# Revit family: Toilet_Seat-Elongated_Closed_Front-KOHLER-PATIO-K-10614IN-1
name_source: partatom
category: Specialty Equipment
units: mm (PartAtom-declared; Revit-internal decimal feet)

## family parameters
Cut with Voids When Loaded = No
Host = Face
OmniClass Number = 23.31.19.19
OmniClass Title = Water Closets
Part Type = Normal
Room Calculation Point = No
Round Connector Dimension = Use Diameter
Shared = No

## types (3) — shared parameters
ADA Compliant = No
Assembly Code = C1030200
Date Modified = 05/16/2024
Default Elevation = 15"
Description = Quiet-Close Toilet Seat
Height = 2 3/8"
Length = 18 1/8"
Manufacturer = Kohler Co.
Master Format 2014 = 10 28 00
Master Format 2014 Name = Toilet, Bath, and Laundry Accessories
Material = Plastic
Product Name = Patio
URL = https://www.kohler.co.in
WaterSense Certified = No
Width = 14 13/16"

## per-type parameters (varying)
| type | Finish | Model | Type |
| 0-White | Kohler-Plastic-0-White | K-10614IN-0 | 1 |
| 47-Almond | Kohler-Plastic-47-Almond | K-10614IN-47 | 3 |
| 7-Black Black | Kohler-Plastic-7-Black_Black | K-10614IN-7 | 2 |

## geometry (parser evidence)
native form markers: Sweep x4
no freeform markers — native parametric forms only
